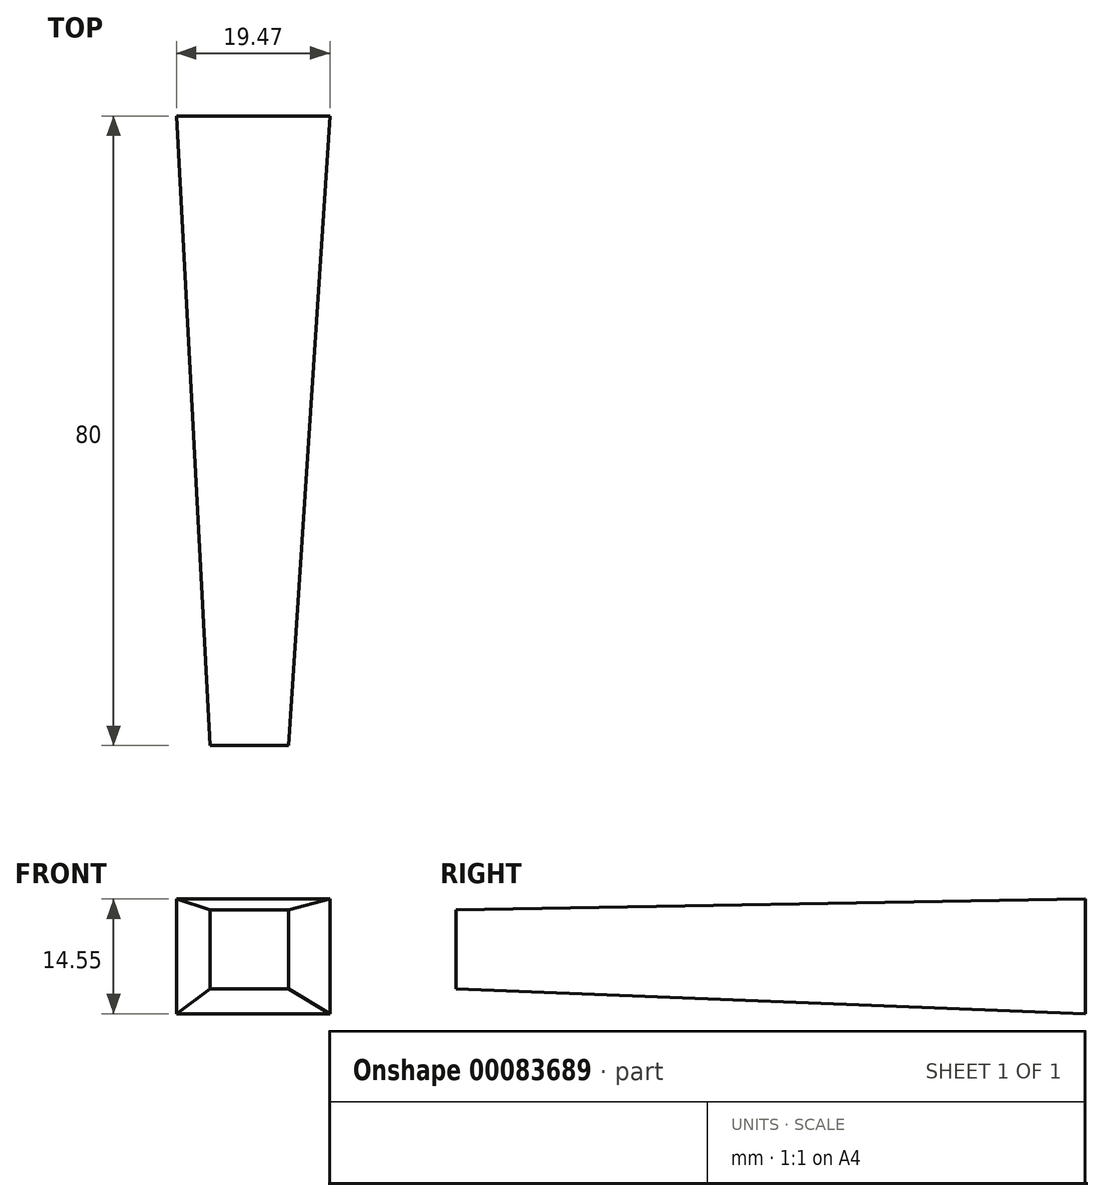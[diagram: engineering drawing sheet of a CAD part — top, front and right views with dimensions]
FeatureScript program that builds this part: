
annotation { "Feature Type Name" : "Feature", "Feature Type Description" : "" }
export const myFeature = defineFeature(function(context is Context, id is Id, definition is map)
    precondition{}
    {
        {
            var Q0;
            Q0=qCreatedBy(makeId("Front.planeOp"),FACE);
            var sketch = newSketch(context, id + "F0", { "sketchPlane" : qUnion([Q0])});
            skLineSegment(sketch, "E0.bottom", {"start": v(0, 0) * mm, "end": v(-19.47, 0) * mm});
            skLineSegment(sketch, "E0.top", {"start": v(0, 14.55) * mm, "end": v(-19.47, 14.55) * mm});
            skLineSegment(sketch, "E0.left", {"start": v(0, 0) * mm, "end": v(0, 14.55) * mm});
            skLineSegment(sketch, "E0.right", {"start": v(-19.47, 0) * mm, "end": v(-19.47, 14.55) * mm});
            skSolve(sketch);
        }
        {
            var Q0;
            Q0=qCreatedBy(makeId("Front.planeOp"),FACE);
            cPlane(context, id + "F1", {"entities" : qUnion([Q0]), "cplaneType" : CPlaneType.OFFSET, "offset" : 80 * mm, "width" : 150 * mm, "height" : 150 * mm});
        }
        {
            var Q0;
            Q0=qCreatedBy(id+"F1.planeOp",FACE);
            var sketch = newSketch(context, id + "F2", { "sketchPlane" : qUnion([Q0])});
            skLineSegment(sketch, "E1.bottom", {"start": v(-15.23, 13.18) * mm, "end": v(-5.23, 13.18) * mm});
            skLineSegment(sketch, "E1.top", {"start": v(-15.23, 3.18) * mm, "end": v(-5.23, 3.18) * mm});
            skLineSegment(sketch, "E1.left", {"start": v(-15.23, 13.18) * mm, "end": v(-15.23, 3.18) * mm});
            skLineSegment(sketch, "E1.right", {"start": v(-5.23, 13.18) * mm, "end": v(-5.23, 3.18) * mm});
            skSolve(sketch);
        }
        {
            var Q0;
            Q0=makeQuery(id+"F2.imprint","IMPRINT",FACE,{"disambiguationData":[TD([[makeQuery(id+"F2.imprint","IMPRINT",EDGE,{"derivedFrom":sQuery(id+"F2.wireOp",EDGE,"E1.bottom")}),-1.0]])]});
            var Q1;
            Q1=makeQuery(id+"F0.imprint","IMPRINT",FACE,{"disambiguationData":[TD([[makeQuery(id+"F0.imprint","IMPRINT",EDGE,{"derivedFrom":sQuery(id+"F0.wireOp",EDGE,"E0.bottom")}),-1.0]])]});
            loft(context, id + "F3", {"sheetProfilesArray" : [{ "sheetProfileEntities" : qUnion([Q0]) }, { "sheetProfileEntities" : qUnion([Q1]) }]});
        }
    });
